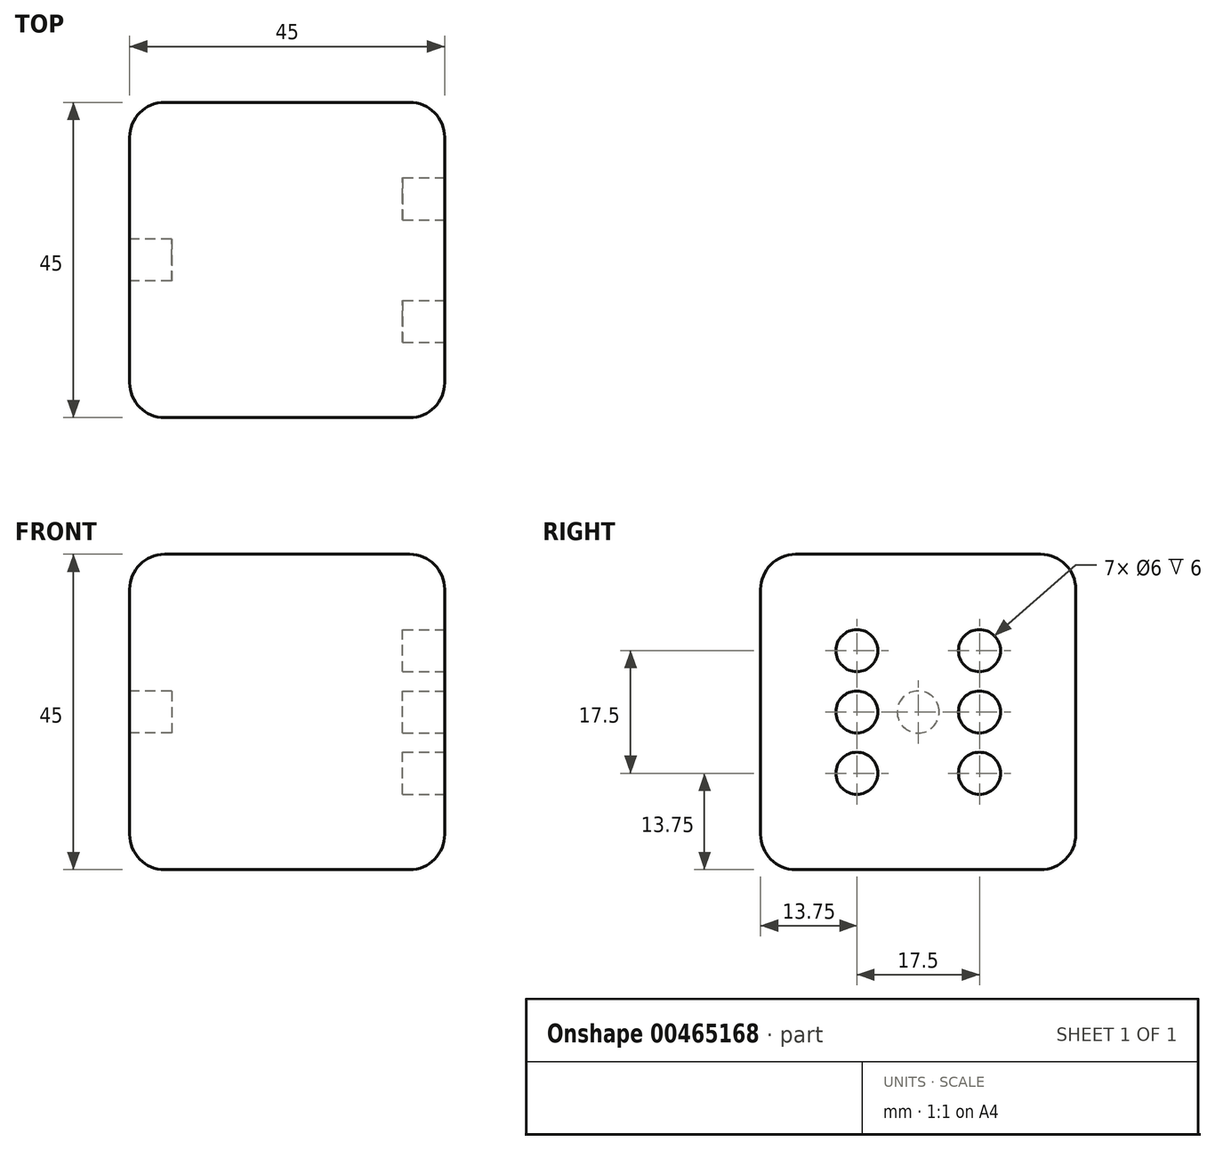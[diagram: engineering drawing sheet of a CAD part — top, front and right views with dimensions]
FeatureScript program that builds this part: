
annotation { "Feature Type Name" : "Feature", "Feature Type Description" : "" }
export const myFeature = defineFeature(function(context is Context, id is Id, definition is map)
    precondition{}
    {
        {
            var Q0;
            Q0=qCreatedBy(makeId("Front.planeOp"),FACE);
            var sketch = newSketch(context, id + "F0", { "sketchPlane" : qUnion([Q0])});
            skLineSegment(sketch, "E0.bottom", {"start": v(-17.5, 22.5) * mm, "end": v(17.5, 22.5) * mm});
            skLineSegment(sketch, "E0.top", {"start": v(-17.5, -22.5) * mm, "end": v(17.5, -22.5) * mm});
            skLineSegment(sketch, "E0.left", {"start": v(-22.5, 17.5) * mm, "end": v(-22.5, -17.5) * mm});
            skLineSegment(sketch, "E0.right", {"start": v(22.5, 17.5) * mm, "end": v(22.5, -17.5) * mm});
            skPoint(sketch, "E0.middle", {"position": v(0, 0) * mm});
            skPoint(sketch, "E1.visualSharp", {"position": v(-22.5, 22.5) * mm});
            skArc(sketch, "E1.filletArc", {"start": v(-17.5, 22.5) * mm, "mid": v(-21.04, 21.04) * mm, "end": v(-22.5, 17.5) * mm});
            skPoint(sketch, "E2.visualSharp", {"position": v(-22.5, -22.5) * mm});
            skArc(sketch, "E2.filletArc", {"start": v(-22.5, -17.5) * mm, "mid": v(-21.04, -21.04) * mm, "end": v(-17.5, -22.5) * mm});
            skPoint(sketch, "E3.visualSharp", {"position": v(22.5, -22.5) * mm});
            skArc(sketch, "E3.filletArc", {"start": v(17.5, -22.5) * mm, "mid": v(21.04, -21.04) * mm, "end": v(22.5, -17.5) * mm});
            skPoint(sketch, "E4.visualSharp", {"position": v(22.5, 22.5) * mm});
            skArc(sketch, "E4.filletArc", {"start": v(22.5, 17.5) * mm, "mid": v(21.04, 21.04) * mm, "end": v(17.5, 22.5) * mm});
            skSolve(sketch);
        }
        {
            var Q0;
            Q0=makeQuery(id+"F0.imprint","IMPRINT",FACE,{"disambiguationData":[TD([[makeQuery(id+"F0.imprint","IMPRINT",EDGE,{"derivedFrom":sQuery(id+"F0.wireOp",EDGE,"E0.bottom")}),-1.0]])]});
            extrude(context, id + "F1", {"entities" : qUnion([Q0]), "depth" : 45 * mm});
        }
        {
            var Q0;
            Q0=makeQuery(id+"F1.opExtrude","CAP_FACE",FACE,{"disambiguationData":[OSD([sQuery(id+"F0.wireOp",EDGE,"E0.bottom"),sQuery(id+"F0.wireOp",EDGE,"E0.top"),sQuery(id+"F0.wireOp",EDGE,"E0.left"),sQuery(id+"F0.wireOp",EDGE,"E0.right"),sQuery(id+"F0.wireOp",EDGE,"E1.filletArc"),sQuery(id+"F0.wireOp",EDGE,"E2.filletArc"),sQuery(id+"F0.wireOp",EDGE,"E3.filletArc"),sQuery(id+"F0.wireOp",EDGE,"E4.filletArc")])],"isStart":false});
            fillet(context, id + "F2", {"entities" : qUnion([Q0]), "radius" : 5 * mm, "tangentPropagation" : true, "allowEdgeOverflow" : false});
        }
        {
            var Q0;
            Q0=makeQuery(id+"F1.opExtrude","CAP_FACE",FACE,{"disambiguationData":[OSD([sQuery(id+"F0.wireOp",EDGE,"E0.bottom"),sQuery(id+"F0.wireOp",EDGE,"E0.top"),sQuery(id+"F0.wireOp",EDGE,"E0.left"),sQuery(id+"F0.wireOp",EDGE,"E0.right"),sQuery(id+"F0.wireOp",EDGE,"E1.filletArc"),sQuery(id+"F0.wireOp",EDGE,"E2.filletArc"),sQuery(id+"F0.wireOp",EDGE,"E3.filletArc"),sQuery(id+"F0.wireOp",EDGE,"E4.filletArc")])],"isStart":true});
            fillet(context, id + "F3", {"entities" : qUnion([Q0]), "radius" : 5 * mm, "tangentPropagation" : true, "allowEdgeOverflow" : false});
        }
        {
            var Q0;
            Q0=makeQuery(id+"F1.opExtrude","SWEPT_FACE",FACE,{"disambiguationData":[OSD([sQuery(id+"F0.wireOp",EDGE,"E0.left")])]});
            var sketch = newSketch(context, id + "F4", { "sketchPlane" : qUnion([Q0])});
            skPoint(sketch, "E5", {"position": v(5, 0) * mm});
            skPoint(sketch, "E6", {"position": v(40, 0) * mm});
            skPoint(sketch, "E7", {"position": v(22.5, 17.5) * mm});
            skPoint(sketch, "E8", {"position": v(22.5, -17.5) * mm});
            skPoint(sketch, "E9", {"position": v(22.5, 0) * mm});
            skCircle(sketch, "E10", {"center": v(22.5, 0) * mm, "radius": 3 * mm});
            skSolve(sketch);
        }
        {
            var Q0;
            Q0=makeQuery(id+"F4.imprint","IMPRINT",FACE,{"disambiguationData":[TD([[makeQuery(id+"F4.imprint","IMPRINT",EDGE,{"derivedFrom":sQuery(id+"F4.wireOp",EDGE,"E10")}),1.0]])]});
            extrude(context, id + "F5", {"entities" : qUnion([Q0]), "operationType" : NewBodyOperationType.REMOVE, "oppositeDirection" : true, "depth" : 6 * mm});
        }
        {
            var Q0;
            Q0=makeQuery(id+"F1.opExtrude","SWEPT_FACE",FACE,{"disambiguationData":[OSD([sQuery(id+"F0.wireOp",EDGE,"E0.right")])]});
            var sketch = newSketch(context, id + "F6", { "sketchPlane" : qUnion([Q0])});
            skPoint(sketch, "E11", {"position": v(-22.5, 17.5) * mm});
            skPoint(sketch, "E12", {"position": v(-22.5, -17.5) * mm});
            skPoint(sketch, "E13", {"position": v(-40, 0) * mm});
            skPoint(sketch, "E14", {"position": v(-5, 0) * mm});
            skPoint(sketch, "E15", {"position": v(-22.5, 0) * mm});
            skPoint(sketch, "E16", {"position": v(-40, 17.5) * mm});
            skPoint(sketch, "E17", {"position": v(-5, 17.5) * mm});
            skPoint(sketch, "E18", {"position": v(-5, -17.5) * mm});
            skPoint(sketch, "E19", {"position": v(-40, -17.5) * mm});
            skPoint(sketch, "E20", {"position": v(-31.25, 8.75) * mm});
            skPoint(sketch, "E21", {"position": v(-31.25, 0) * mm});
            skPoint(sketch, "E22", {"position": v(-31.25, -8.75) * mm});
            skPoint(sketch, "E23", {"position": v(-13.75, 0) * mm});
            skPoint(sketch, "E24", {"position": v(-13.75, 8.75) * mm});
            skPoint(sketch, "E25", {"position": v(-13.75, -8.75) * mm});
            skPoint(sketch, "E26", {"position": v(-22.5, 8.75) * mm});
            skPoint(sketch, "E27", {"position": v(-22.5, -8.75) * mm});
            skCircle(sketch, "E28", {"center": v(-31.25, 8.75) * mm, "radius": 3 * mm});
            skCircle(sketch, "E29", {"center": v(-31.25, 0) * mm, "radius": 3 * mm});
            skCircle(sketch, "E30", {"center": v(-31.25, -8.75) * mm, "radius": 3 * mm});
            skCircle(sketch, "E31", {"center": v(-13.75, 8.75) * mm, "radius": 3 * mm});
            skCircle(sketch, "E32", {"center": v(-13.75, 0) * mm, "radius": 3 * mm});
            skCircle(sketch, "E33", {"center": v(-13.75, -8.75) * mm, "radius": 3 * mm});
            skSolve(sketch);
        }
        {
            var Q0;
            Q0=makeQuery(id+"F6.imprint","IMPRINT",FACE,{"disambiguationData":[TD([[makeQuery(id+"F6.imprint","IMPRINT",EDGE,{"derivedFrom":sQuery(id+"F6.wireOp",EDGE,"E28")}),1.0]])]});
            var Q1;
            Q1=makeQuery(id+"F6.imprint","IMPRINT",FACE,{"disambiguationData":[TD([[makeQuery(id+"F6.imprint","IMPRINT",EDGE,{"derivedFrom":sQuery(id+"F6.wireOp",EDGE,"E29")}),1.0]])]});
            var Q2;
            Q2=makeQuery(id+"F6.imprint","IMPRINT",FACE,{"disambiguationData":[TD([[makeQuery(id+"F6.imprint","IMPRINT",EDGE,{"derivedFrom":sQuery(id+"F6.wireOp",EDGE,"E30")}),1.0]])]});
            var Q3;
            Q3=makeQuery(id+"F6.imprint","IMPRINT",FACE,{"disambiguationData":[TD([[makeQuery(id+"F6.imprint","IMPRINT",EDGE,{"derivedFrom":sQuery(id+"F6.wireOp",EDGE,"E33")}),1.0]])]});
            var Q4;
            Q4=makeQuery(id+"F6.imprint","IMPRINT",FACE,{"disambiguationData":[TD([[makeQuery(id+"F6.imprint","IMPRINT",EDGE,{"derivedFrom":sQuery(id+"F6.wireOp",EDGE,"E32")}),1.0]])]});
            var Q5;
            Q5=makeQuery(id+"F6.imprint","IMPRINT",FACE,{"disambiguationData":[TD([[makeQuery(id+"F6.imprint","IMPRINT",EDGE,{"derivedFrom":sQuery(id+"F6.wireOp",EDGE,"E31")}),1.0]])]});
            extrude(context, id + "F7", {"entities" : qUnion([Q0, Q1, Q2, Q3, Q4, Q5]), "operationType" : NewBodyOperationType.REMOVE, "oppositeDirection" : true, "depth" : 6 * mm});
        }
    });
